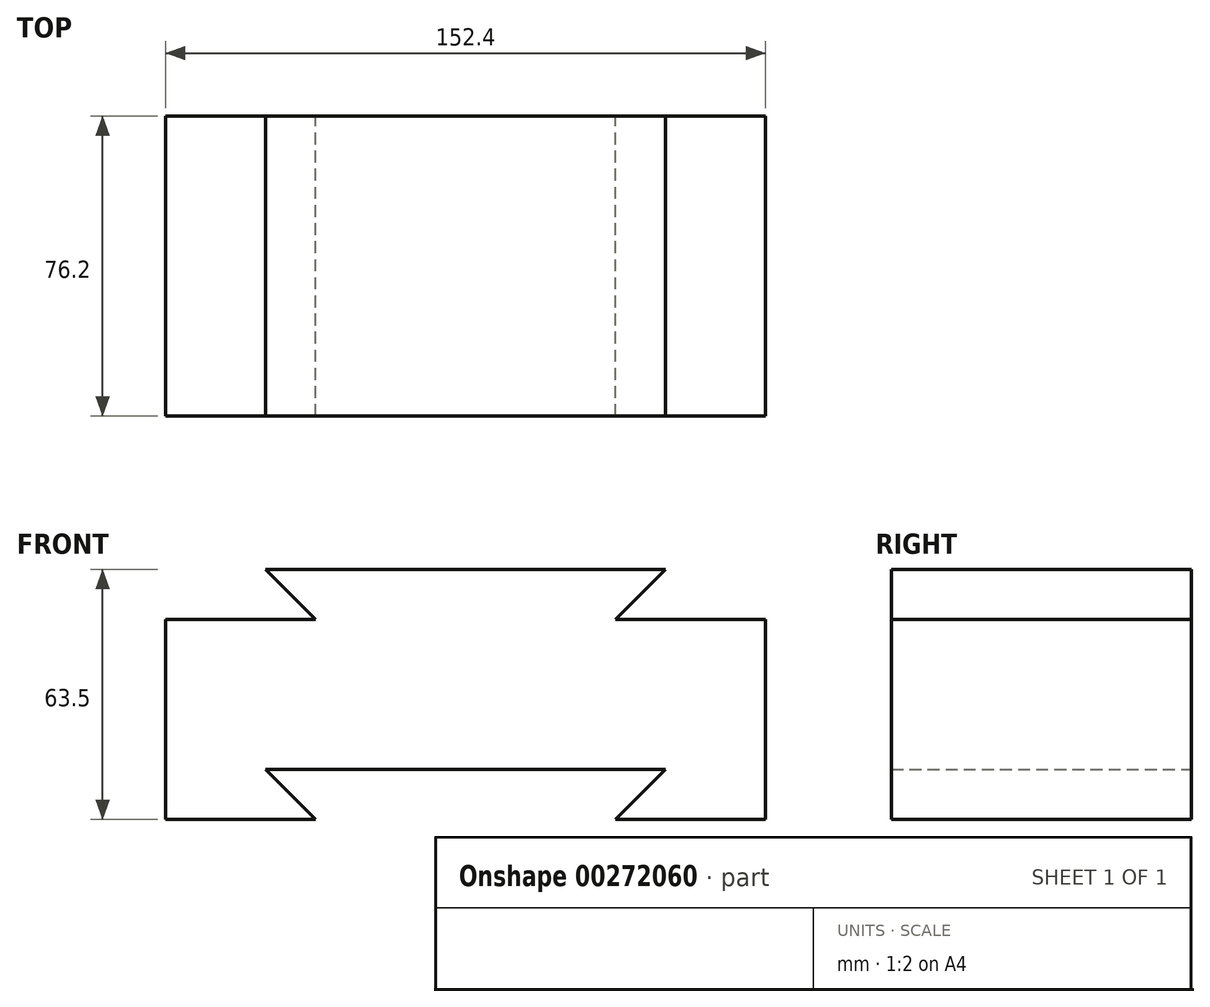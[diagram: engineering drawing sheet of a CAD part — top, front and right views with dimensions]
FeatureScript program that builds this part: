
annotation { "Feature Type Name" : "Feature", "Feature Type Description" : "" }
export const myFeature = defineFeature(function(context is Context, id is Id, definition is map)
    precondition{}
    {
        {
            var Q0;
            Q0=qCreatedBy(makeId("Front.planeOp"),FACE);
            var sketch = newSketch(context, id + "F0", { "sketchPlane" : qUnion([Q0])});
            skLineSegment(sketch, "E0", {"start": v(-45.42, 48.85) * mm, "end": v(56.18, 48.85) * mm});
            skLineSegment(sketch, "E1", {"start": v(-45.42, 48.85) * mm, "end": v(-32.72, 36.15) * mm});
            skLineSegment(sketch, "E2", {"start": v(43.48, 36.15) * mm, "end": v(56.18, 48.85) * mm});
            skLineSegment(sketch, "E3", {"start": v(43.48, 36.15) * mm, "end": v(81.58, 36.15) * mm});
            skLineSegment(sketch, "E4", {"start": v(-32.72, 36.15) * mm, "end": v(-70.82, 36.15) * mm});
            skLineSegment(sketch, "E5", {"start": v(-70.82, 36.15) * mm, "end": v(-70.82, -14.65) * mm});
            skLineSegment(sketch, "E6", {"start": v(81.58, 36.15) * mm, "end": v(81.58, -14.65) * mm});
            skLineSegment(sketch, "E7", {"start": v(-70.82, -14.65) * mm, "end": v(-32.72, -14.65) * mm});
            skLineSegment(sketch, "E8", {"start": v(81.58, -14.65) * mm, "end": v(43.48, -14.65) * mm});
            skLineSegment(sketch, "E9", {"start": v(56.17, -1.95) * mm, "end": v(43.48, -14.65) * mm});
            skLineSegment(sketch, "E10", {"start": v(-45.42, -1.95) * mm, "end": v(-32.72, -14.65) * mm});
            skLineSegment(sketch, "E11", {"start": v(-45.42, -1.95) * mm, "end": v(56.17, -1.95) * mm});
            skSolve(sketch);
        }
        {
            var Q0;
            Q0=makeQuery(id+"F0.imprint","IMPRINT",FACE,{"disambiguationData":[TD([[makeQuery(id+"F0.imprint","IMPRINT",EDGE,{"derivedFrom":sQuery(id+"F0.wireOp",EDGE,"E0")}),-1.0]])]});
            extrude(context, id + "F1", {"entities" : qUnion([Q0]), "depth" : 76.2 * mm});
        }
    });
